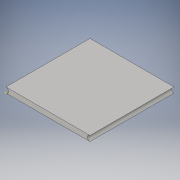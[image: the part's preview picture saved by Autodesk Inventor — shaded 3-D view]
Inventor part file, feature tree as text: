
AUTODESK INVENTOR PART (.ipt)
format: ipt  version: 2016 (Build 200138000, 138)  size: 90,624 bytes
history: native  units: in
note: dims shown in document units (in); Inventor stores cm internally (conversion verified against a paired STEP export)
features: sketch x2, extrude x1
ambient origin geometry x8: Origin, YZ Plane, XZ Plane, XY Plane, X Axis, Y Axis, Z Axis, Center Point
bodies: Solid1 (feature_tree)
feature tree (3):
  sketch  "Sketch1"  dims[d0=2.4409in d1=0.1535in]
  extrude  "Extrusion1"  Depth=0.1535in
  sketch  "Sketch2"  dims[d2=2.4409in d3=0.0in]
